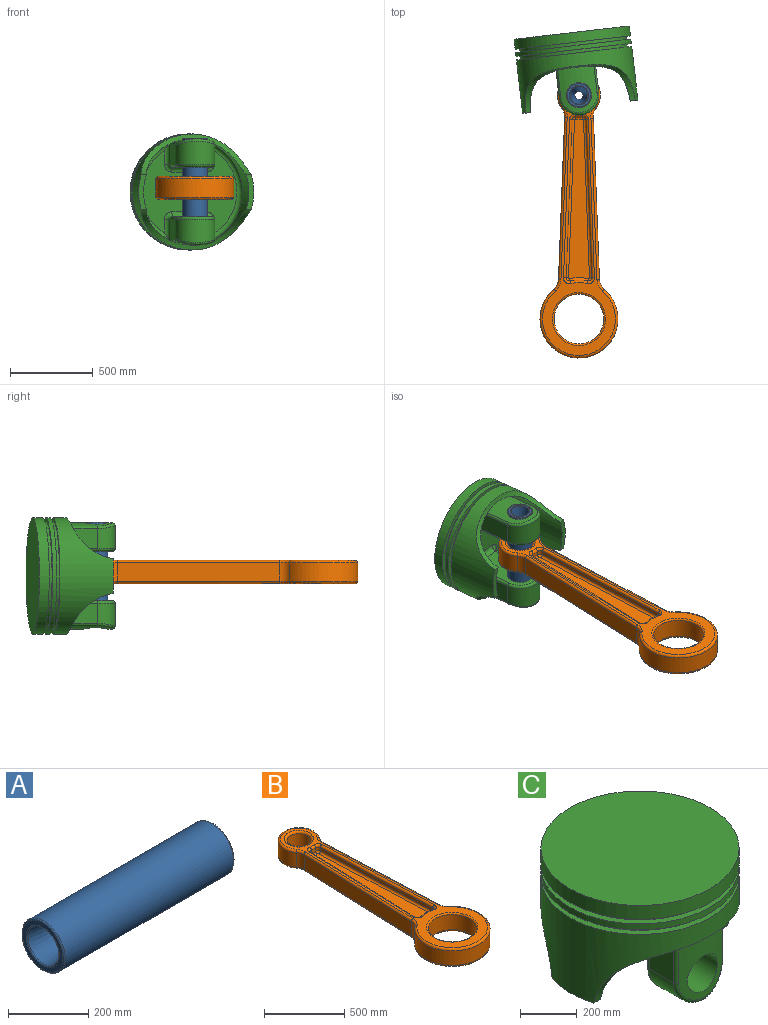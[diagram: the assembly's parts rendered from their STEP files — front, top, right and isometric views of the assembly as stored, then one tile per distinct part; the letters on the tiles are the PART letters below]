
ASSEMBLY  parts=3 mates=2
PART A: 10 faces, bbox 600x162.4x162.4 mm
  f0: cylinder r=75mm len=592mm, axis (-1,0,0), area 278973.4mm2, adj f1,f2
  f1: torus R=71mm, axis (1,0,0), area 2903.5mm2, adj f0,f3
  f2: torus R=71mm, axis (1,0,0), area 2903.5mm2, adj f0,f4
  f3: plane 142.01x142.01mm, normal (-1,0,0), area 5105.6mm2, adj f1,f5
  f4: plane 142.01x142.01mm, normal (1,0,0), area 5105.6mm2, adj f2,f6
  f5: torus R=58.44mm, axis (1,0,0), area 2003mm2, adj f3,f7
  f6: torus R=58.44mm, axis (1,0,0), area 2003mm2, adj f4,f8
  f7: cone r=25mm half-angle=8.5deg, axis (-1,0,0), area 49642.9mm2, adj f5,f9
  f8: cone r=25mm half-angle=8.5deg, axis (1,0,0), area 49642.9mm2, adj f6,f9
  f9: cylinder r=25mm len=200mm, axis (-1,0,0), area 31415.9mm2, adj f7,f8
PART B: 82 faces, bbox 508.7x1745.1x140 mm
  f0: plane 963.42x126.21mm, normal (0,0,-1), area 86369.2mm2, adj f2,f3,f4,f5,f6,f7,f8,f9
  f1: plane 963.42x126.21mm, normal (0,0,1), area 86369.2mm2, adj f10,f11,f12,f13,f14,f15,f16,f17
  f2: torus R=5mm, axis (0,0,1), area 577.2mm2, adj f0,f3,f9,f18
  f3: torus R=145mm, axis (0,0,1), area 946.4mm2, adj f0,f2,f4,f19
  f4: torus R=5mm, axis (0,0,1), area 575.6mm2, adj f0,f3,f5,f20
  f5: cylinder r=15mm len=953.87mm, axis (-0.04,-1,0), area 22477.9mm2, adj f0,f4,f6,f21
  f6: torus R=5mm, axis (0,0,1), area 630.3mm2, adj f0,f5,f7,f22
  f7: torus R=250mm, axis (0,0,1), area 2604.4mm2, adj f0,f6,f8,f23
  f8: torus R=5mm, axis (0,0,1), area 630.1mm2, adj f0,f7,f9,f24
  f9: cylinder r=15mm len=953.96mm, axis (-0.04,1,0), area 22479.7mm2, adj f0,f2,f8,f25
  f10: torus R=5mm, axis (0,0,1), area 630.3mm2, adj f1,f11,f17,f32
  f11: cylinder r=15mm len=953.87mm, axis (0.04,1,0), area 22477.9mm2, adj f1,f10,f12,f33
  f12: torus R=5mm, axis (0,0,1), area 575.6mm2, adj f1,f11,f13,f34
  f13: torus R=145mm, axis (0,0,1), area 946.4mm2, adj f1,f12,f14,f35
  f14: torus R=5mm, axis (0,0,1), area 577.2mm2, adj f1,f13,f15,f36
  f15: cylinder r=15mm len=953.96mm, axis (0.04,-1,0), area 22479.7mm2, adj f1,f14,f16,f37
  f16: torus R=5mm, axis (0,0,1), area 630.1mm2, adj f1,f15,f17,f38
  f17: torus R=250mm, axis (0,0,1), area 2604.4mm2, adj f1,f10,f16,f39
  f18: cylinder r=20mm len=25mm, axis (0,0,-1), area 841.9mm2, adj f2,f19,f25,f40
  f19: cylinder r=130mm len=38.41mm, axis (0,0,-1), area 963.8mm2, adj f3,f18,f20,f41
  f20: cylinder r=20mm len=25mm, axis (0,0,-1), area 839.5mm2, adj f4,f19,f21,f42
  f21: plane 953.3x36.23mm, normal (1,-0.04,0), area 23849.8mm2, adj f5,f20,f22,f43
  f22: cylinder r=20mm len=25mm, axis (0,0,-1), area 919.3mm2, adj f6,f21,f23,f44
  f23: cylinder r=235mm len=107.08mm, axis (0,0,-1), area 2700.7mm2, adj f7,f22,f24,f45
  f24: cylinder r=20mm len=25mm, axis (0,0,-1), area 919mm2, adj f8,f23,f25,f46
  f25: plane 953.4x35.65mm, normal (-1,-0.04,0), area 23851.7mm2, adj f9,f18,f24,f47
  f26: cylinder r=130mm len=260mm, axis (0,0,-1), area 63734.1mm2, adj f27,f29,f51,f58
  f27: cylinder r=80mm len=110mm, axis (0,0,-1), area 6121.7mm2, adj f26,f28,f50,f59
  f28: plane 981.17x110mm, normal (-1,0.04,0), area 108007.1mm2, adj f27,f54,f57,f60
  f29: cylinder r=80mm len=110mm, axis (0,0,-1), area 7214.5mm2, adj f26,f52,f56,f62
  f30: cylinder r=75mm len=150mm, axis (0,0,-1), area 51836.3mm2, adj f49,f63
  f31: cylinder r=150mm len=300mm, axis (0,0,1), area 108384.9mm2, adj f48,f64
  f32: cylinder r=20mm len=25mm, axis (0,0,-1), area 919.3mm2, adj f10,f33,f39,f65
  f33: plane 953.3x36.23mm, normal (1,-0.04,0), area 23849.8mm2, adj f11,f32,f34,f66
  f34: cylinder r=20mm len=25mm, axis (0,0,-1), area 839.5mm2, adj f12,f33,f35,f67
  f35: cylinder r=130mm len=38.41mm, axis (0,0,-1), area 963.8mm2, adj f13,f34,f36,f68
  f36: cylinder r=20mm len=25mm, axis (0,0,-1), area 841.9mm2, adj f14,f35,f37,f69
  f37: plane 953.4x35.65mm, normal (-1,-0.04,0), area 23851.7mm2, adj f15,f36,f38,f70
  f38: cylinder r=20mm len=25mm, axis (0,0,-1), area 919mm2, adj f16,f37,f39,f71
  f39: cylinder r=235mm len=107.08mm, axis (0,0,-1), area 2700.7mm2, adj f17,f32,f38,f72
  f40: torus R=35mm, axis (0,0,1), area 1009.7mm2, adj f18,f41,f47,f74
  f41: torus R=115mm, axis (0,0,1), area 870.3mm2, adj f19,f40,f42,f74
  f42: torus R=35mm, axis (0,0,1), area 1006.9mm2, adj f20,f41,f43,f74
  f43: cylinder r=15mm len=953.87mm, axis (0.04,1,0), area 22477.9mm2, adj f21,f42,f44,f74
  f44: torus R=35mm, axis (0,0,1), area 1102.5mm2, adj f22,f43,f45,f74
  f45: torus R=220mm, axis (0,0,1), area 2486.3mm2, adj f23,f44,f46,f74
  f46: torus R=35mm, axis (0,0,1), area 1102.2mm2, adj f24,f45,f47,f74
  f47: cylinder r=15mm len=953.96mm, axis (0.04,-1,0), area 22479.7mm2, adj f25,f40,f46,f74
  f48: torus R=165mm, axis (0,0,1), area 23013.6mm2, adj f31,f74
  f49: torus R=90mm, axis (0,0,1), area 11910.2mm2, adj f30,f74
  f50: torus R=95mm, axis (0,0,1), area 1400.6mm2, adj f27,f51,f54,f74
  f51: torus R=115mm, axis (0,0,1), area 13079.4mm2, adj f26,f50,f52,f74
  f52: torus R=95mm, axis (0,0,1), area 1640mm2, adj f29,f51,f53,f74
  f53: cylinder r=15mm len=969.87mm, axis (-0.04,1,0), area 22842.2mm2, adj f52,f55,f56,f74
  f54: cylinder r=15mm len=981.74mm, axis (-0.04,-1,0), area 23135.1mm2, adj f28,f50,f74,f75
  f55: torus R=95mm, axis (0,0,1), area 1720.1mm2, adj f53,f74,f76,f79
  f56: plane 969.31x110mm, normal (1,0.04,0), area 106698.7mm2, adj f29,f53,f61,f76
  f57: cylinder r=80mm len=110mm, axis (0,0,-1), area 7308.5mm2, adj f28,f75,f77,f81
  f58: torus R=115mm, axis (0,0,1), area 13079.4mm2, adj f26,f59,f62,f78
  f59: torus R=95mm, axis (0,0,1), area 1400.6mm2, adj f27,f58,f60,f78
  f60: cylinder r=15mm len=981.74mm, axis (0.04,1,0), area 23135.1mm2, adj f28,f59,f77,f78
  f61: cylinder r=15mm len=969.87mm, axis (0.04,-1,0), area 22842.2mm2, adj f56,f62,f73,f78
  f62: torus R=95mm, axis (0,0,1), area 1640mm2, adj f29,f58,f61,f78
  f63: torus R=90mm, axis (0,0,1), area 11910.2mm2, adj f30,f78
  f64: torus R=160mm, axis (0,0,1), area 15163mm2, adj f31,f78
  f65: torus R=35mm, axis (0,0,1), area 1102.5mm2, adj f32,f66,f72,f78
  f66: cylinder r=15mm len=953.87mm, axis (-0.04,-1,0), area 22477.9mm2, adj f33,f65,f67,f78
  f67: torus R=35mm, axis (0,0,1), area 1006.9mm2, adj f34,f66,f68,f78
  f68: torus R=115mm, axis (0,0,1), area 870.3mm2, adj f35,f67,f69,f78
  f69: torus R=35mm, axis (0,0,1), area 1009.7mm2, adj f36,f68,f70,f78
  f70: cylinder r=15mm len=953.96mm, axis (-0.04,1,0), area 22479.7mm2, adj f37,f69,f71,f78
  f71: torus R=35mm, axis (0,0,1), area 1102.2mm2, adj f38,f70,f72,f78
  f72: torus R=220mm, axis (0,0,1), area 2486.3mm2, adj f39,f65,f71,f78
  f73: torus R=95mm, axis (0,0,1), area 1720.1mm2, adj f61,f76,f78,f80
  f74: plane 1685.24x440.12mm, normal (0,0,-1), area 117285.6mm2, adj f40,f41,f42,f43,f44,f45,f46,f47
  f75: torus R=95mm, axis (0,0,1), area 1672.1mm2, adj f54,f57,f74,f79
  f76: cylinder r=80mm len=110mm, axis (0,0,-1), area 7527mm2, adj f55,f56,f73,f81
  f77: torus R=95mm, axis (0,0,1), area 1672.1mm2, adj f57,f60,f78,f80
  f78: plane 1685.24x440.12mm, normal (0,0,1), area 122390.9mm2, adj f58,f59,f60,f61,f62,f63,f64,f65
  f79: torus R=220mm, axis (0,0,1), area 26386.4mm2, adj f55,f74,f75,f81
  f80: torus R=220mm, axis (0,0,1), area 26386.4mm2, adj f73,f77,f78,f81
  f81: cylinder r=235mm len=470mm, axis (0,0,-1), area 126111.4mm2, adj f57,f76,f79,f80
PART C: 53 faces, bbox 700x700x509.9 mm
  f0: plane 700.01x700.01mm, normal (0,0,1), area 384836.7mm2, adj f1
  f1: cylinder r=350mm len=700mm, axis (0,0,-1), area 131946.9mm2, adj f0,f2
  f2: plane 700.01x700.01mm, normal (0,0,-1), area 53013.2mm2, adj f1,f3
  f3: cylinder r=325mm len=650mm, axis (0,0,-1), area 40840.7mm2, adj f2,f4
  f4: plane 700.01x700.01mm, normal (0,0,1), area 53013.2mm2, adj f3,f5
  f5: cylinder r=350mm len=700mm, axis (0,0,-1), area 55637.6mm2, adj f4,f7
  f6: cylinder r=75mm len=170mm, axis (0,-1,0), area 80110.6mm2, adj f8,f25
  f7: plane 700.01x700.01mm, normal (0,0,-1), area 53013.2mm2, adj f5,f17
  f8: plane 375x210mm, normal (0,1,0), area 56346.2mm2, adj f6,f9,f10,f13,f18
  f9: torus R=105mm, axis (0,-1,0), area 8479.2mm2, adj f8,f10,f18,f19
  f10: cylinder r=15mm len=270mm, axis (0,0,-1), area 6361.7mm2, adj f8,f9,f14,f23
  f11: bspline ~240x120mm, area 7671mm2, adj f19,f24,f25,f26
  f12: torus R=45mm, axis (0,0,1), area 1917.3mm2, adj f13,f18,f20,f27
  f13: cylinder r=30mm len=210mm, axis (-1,0,0), area 9896mm2, adj f8,f12,f14,f27
  f14: torus R=45mm, axis (0,0,1), area 1917.3mm2, adj f10,f13,f22,f27
  f15: cylinder r=75mm len=170mm, axis (0,-1,0), area 80110.6mm2, adj f29,f52
  f16: cylinder r=30mm len=210mm, axis (1,0,0), area 9896mm2, adj f21,f27,f28,f29
  f17: cylinder r=325mm len=650mm, axis (0,0,-1), area 40840.7mm2, adj f7,f31
  f18: cylinder r=15mm len=270mm, axis (0,0,1), area 6361.7mm2, adj f8,f9,f12,f32
  f19: cylinder r=120mm len=240mm, axis (0,1,0), area 45750.3mm2, adj f9,f11,f23,f32
  f20: cylinder r=30mm len=131.65mm, axis (0,1,0), area 5062.1mm2, adj f12,f27,f32,f33
  f21: torus R=45mm, axis (0,0,1), area 1917.3mm2, adj f16,f27,f34,f35
  f22: cylinder r=30mm len=131.65mm, axis (0,-1,0), area 5062.1mm2, adj f14,f23,f27,f36
  f23: plane 270x131.65mm, normal (-1,0,0), area 33901.6mm2, adj f10,f19,f22,f24,f37,f45
  f24: cylinder r=15mm len=163mm, axis (0,0,1), area 2932.3mm2, adj f11,f23,f25,f37
  f25: cylinder r=320mm len=268mm, axis (0,0,1), area 37327.5mm2, adj f6,f11,f24,f26,f37
  f26: cylinder r=15mm len=163mm, axis (0,0,1), area 2932.3mm2, adj f11,f25,f32,f37
  f27: plane 580.01x496.4mm, normal (0,0,-1), area 172045.2mm2, adj f12,f13,f14,f16,f20,f21,f22,f28
  f28: torus R=45mm, axis (0,0,1), area 1917.3mm2, adj f16,f27,f38,f39
  f29: plane 375x210mm, normal (0,-1,0), area 56346.2mm2, adj f15,f16,f30,f34,f39
  f30: torus R=105mm, axis (0,1,0), area 8479.2mm2, adj f29,f34,f39,f40
  f31: plane 700.01x700.01mm, normal (0,0,1), area 53013.2mm2, adj f17,f41
  f32: plane 270x131.65mm, normal (1,0,0), area 33901.6mm2, adj f18,f19,f20,f26,f37,f43
  f33: torus R=290mm, axis (0,0,1), area 32281.9mm2, adj f20,f27,f38,f43
  f34: cylinder r=15mm len=270mm, axis (0,0,1), area 6361.7mm2, adj f21,f29,f30,f44
  f35: cylinder r=30mm len=131.65mm, axis (0,-1,0), area 5062.1mm2, adj f21,f27,f36,f44
  f36: torus R=290mm, axis (0,0,1), area 32281.9mm2, adj f22,f27,f35,f45
  f37: cylinder r=300mm len=668.26mm, axis (-1,0,0), area 34186.8mm2, adj f23,f24,f25,f26,f32,f41,f42,f43
  f38: cylinder r=30mm len=131.65mm, axis (0,1,0), area 5062.1mm2, adj f27,f28,f33,f47
  f39: cylinder r=15mm len=270mm, axis (0,0,-1), area 6361.7mm2, adj f28,f29,f30,f47
  f40: cylinder r=120mm len=240mm, axis (0,1,0), area 45750.3mm2, adj f30,f44,f47,f48
  f41: cylinder r=350mm len=700mm, axis (0,0,-1), area 359061.9mm2, adj f31,f37,f42,f46,f50
  f42: plane 208.4x47.44mm, normal (0,0,-1), area 6357.4mm2, adj f37,f41,f43,f50
  f43: cylinder r=320mm len=593.3mm, axis (0,0,-1), area 164685.3mm2, adj f32,f33,f37,f42,f47,f50
  f44: plane 270x131.65mm, normal (-1,0,0), area 33901.6mm2, adj f34,f35,f40,f45,f49,f50
  f45: cylinder r=320mm len=593.3mm, axis (0,0,-1), area 164735.3mm2, adj f23,f36,f37,f44,f46,f50
  f46: plane 208.4x47.44mm, normal (0,0,-1), area 6357.4mm2, adj f37,f41,f45,f50
  f47: plane 270x131.65mm, normal (1,0,0), area 33901.6mm2, adj f38,f39,f40,f43,f50,f51
  f48: bspline ~240x120mm, area 7671mm2, adj f40,f49,f51,f52
  f49: cylinder r=15mm len=163mm, axis (0,0,1), area 2932.3mm2, adj f44,f48,f50,f52
  f50: cylinder r=300mm len=668.26mm, axis (-1,0,0), area 34127.7mm2, adj f41,f42,f43,f44,f45,f46,f47,f49
  f51: cylinder r=15mm len=163mm, axis (0,0,1), area 2932.3mm2, adj f47,f48,f50,f52
  f52: cylinder r=320mm len=268mm, axis (0,0,1), area 37327.5mm2, adj f15,f48,f49,f50,f51
PLACE A rot(axis=(0,-1,0),90deg) t=(232.73,1187.28,1262.77)mm
PLACE B t=(231.16,-78.65,-157.23)mm
PLACE C rot(axis=(-1,-0.06,0.06),90.2deg) t=(1234.15,1232.79,-111.66)mm
MATE revolute C.f6 <-> A.f0  axis (0,0,1) through (232.73,1187.28,209.36)mm
MATE revolute A.f0 <-> B.f3  axis (0,0,-1) through (232.73,1187.28,-87.23)mm
